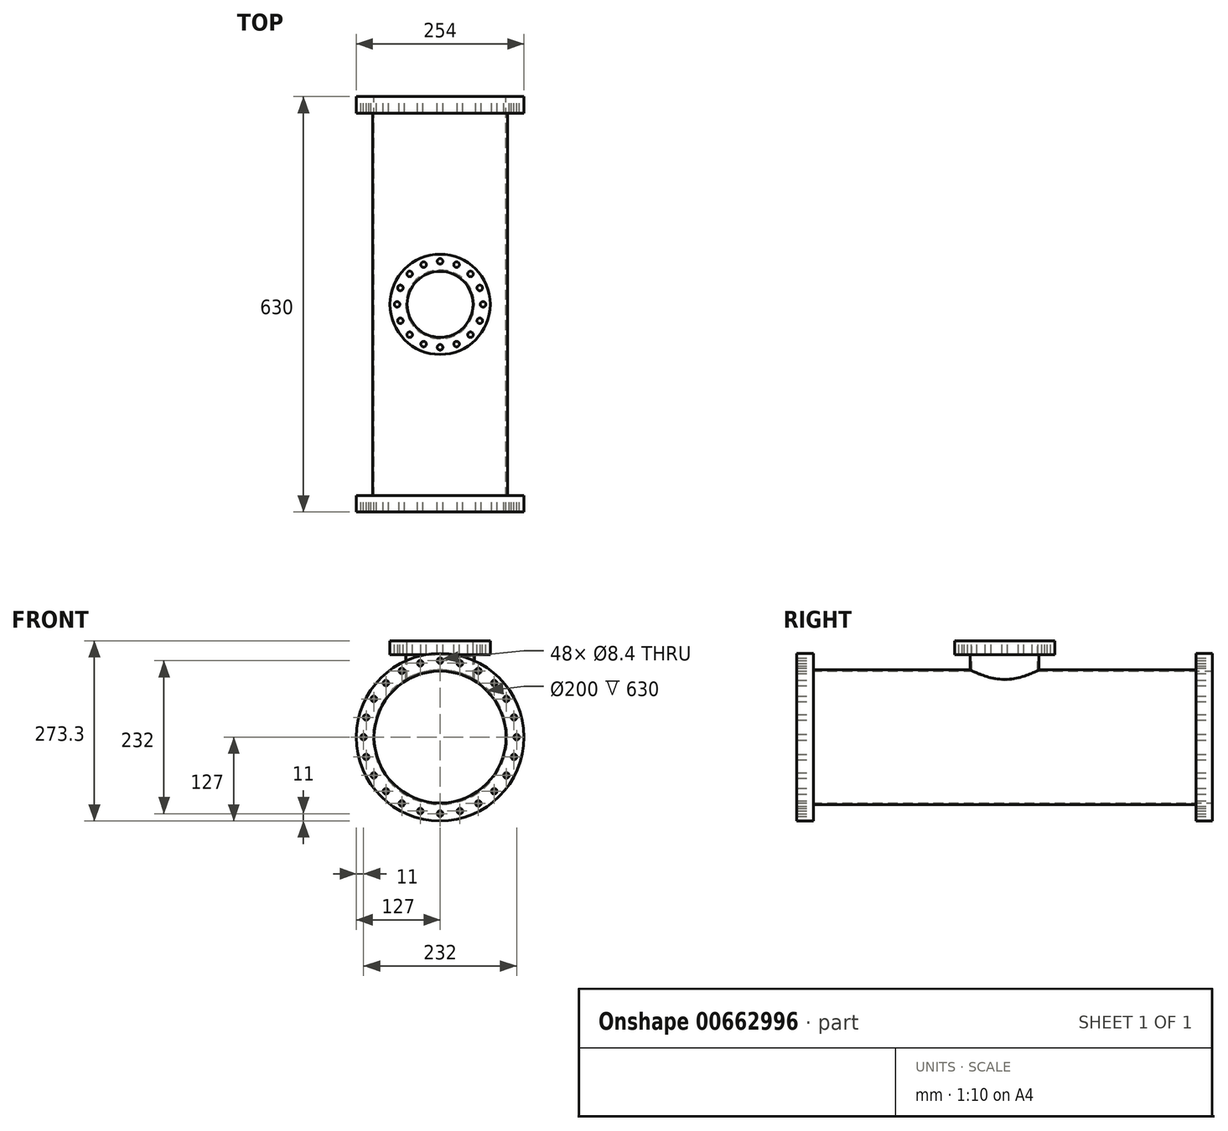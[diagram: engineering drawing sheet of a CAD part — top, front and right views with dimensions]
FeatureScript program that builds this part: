
annotation { "Feature Type Name" : "Feature", "Feature Type Description" : "" }
export const myFeature = defineFeature(function(context is Context, id is Id, definition is map)
    precondition{}
    {
        {
            var Q0;
            Q0=qCreatedBy(makeId("Front.planeOp"),FACE);
            var sketch = newSketch(context, id + "F0", { "sketchPlane" : qUnion([Q0])});
            skCircle(sketch, "E0", {"center": v(0, 0) * mm, "radius": 100 * mm});
            skCircle(sketch, "E1.0", {"center": v(0, 0) * mm, "radius": 102 * mm});
            skSolve(sketch);
        }
        {
            var Q0;
            Q0=makeQuery(id+"F0.imprint","IMPRINT",FACE,{"disambiguationData":[TD([[makeQuery(id+"F0.imprint","IMPRINT",EDGE,{"derivedFrom":sQuery(id+"F0.wireOp",EDGE,"E0")}),-1.0]])]});
            extrude(context, id + "F1", {"entities" : qUnion([Q0]), "depth" : (630 - 50) * mm, "offsetDistance" : 25 * mm});
        }
        {
            var Q0;
            Q0=makeQuery(id+"F1.opExtrude","CAP_FACE",FACE,{"disambiguationData":[OSD([sQuery(id+"F0.wireOp",EDGE,"E0"),sQuery(id+"F0.wireOp",EDGE,"E1.0")])],"isStart":false});
            var sketch = newSketch(context, id + "F2", { "sketchPlane" : qUnion([Q0])});
            skCircle(sketch, "E2", {"center": v(0, 0) * mm, "radius": 127 * mm});
            skSolve(sketch);
        }
        {
            var Q0;
            Q0=makeQuery(id+"F2.imprint","IMPRINT",FACE,{"disambiguationData":[TD([[makeQuery(id+"F2.imprint","IMPRINT",EDGE,{"derivedFrom":makeQuery(id+"F1.opExtrude","CAP_EDGE",EDGE,{"disambiguationData":[OSD([sQuery(id+"F0.wireOp",EDGE,"E0")])],"isStart":false})}),-1.0]])]});
            var Q1;
            Q1=makeQuery(id+"F2.imprint","IMPRINT",FACE,{"disambiguationData":[TD([[makeQuery(id+"F2.imprint","IMPRINT",EDGE,{"derivedFrom":sQuery(id+"F2.wireOp",EDGE,"E2")}),1.0]])]});
            extrude(context, id + "F3", {"entities" : qUnion([Q0, Q1]), "operationType" : NewBodyOperationType.ADD, "depth" : 25 * mm, "offsetDistance" : 25 * mm});
        }
        {
            var Q0;
            Q0=makeQuery(id+"F1.opExtrude","CAP_FACE",FACE,{"disambiguationData":[OSD([sQuery(id+"F0.wireOp",EDGE,"E0"),sQuery(id+"F0.wireOp",EDGE,"E1.0")])],"isStart":true});
            var sketch = newSketch(context, id + "F4", { "sketchPlane" : qUnion([Q0])});
            skCircle(sketch, "E3", {"center": v(0, 0) * mm, "radius": 127 * mm});
            skSolve(sketch);
        }
        {
            var Q0;
            Q0=makeQuery(id+"F4.imprint","IMPRINT",FACE,{"disambiguationData":[TD([[makeQuery(id+"F4.imprint","IMPRINT",EDGE,{"derivedFrom":makeQuery(id+"F1.opExtrude","CAP_EDGE",EDGE,{"disambiguationData":[OSD([sQuery(id+"F0.wireOp",EDGE,"E0")])],"isStart":true})}),1.0]])]});
            var Q1;
            Q1=makeQuery(id+"F4.imprint","IMPRINT",FACE,{"disambiguationData":[TD([[makeQuery(id+"F4.imprint","IMPRINT",EDGE,{"derivedFrom":sQuery(id+"F4.wireOp",EDGE,"E3")}),1.0]])]});
            extrude(context, id + "F5", {"entities" : qUnion([Q0, Q1]), "operationType" : NewBodyOperationType.ADD, "depth" : 25 * mm, "offsetDistance" : 25 * mm});
        }
        {
            var Q0;
            Q0=makeQuery(id+"F5.opExtrude","CAP_FACE",FACE,{"disambiguationData":[OSD([sQuery(id+"F0.wireOp",EDGE,"E0"),sQuery(id+"F4.wireOp",EDGE,"E3")])],"isStart":false});
            var sketch = newSketch(context, id + "F6", { "sketchPlane" : qUnion([Q0])});
            skCircle(sketch, "E4", {"center": v(0, 0) * mm, "radius": 116 * mm, "construction": true});
            skPoint(sketch, "E5", {"position": v(0, 116) * mm});
            skPoint(sketch, "E6.1.0", {"position": v(-30.02, 112.05) * mm});
            skPoint(sketch, "E6.2.0", {"position": v(-58, 100.46) * mm});
            skPoint(sketch, "E6.3.0", {"position": v(-82.02, 82.02) * mm});
            skPoint(sketch, "E6.4.0", {"position": v(-100.46, 58) * mm});
            skPoint(sketch, "E6.5.0", {"position": v(-112.05, 30.02) * mm});
            skPoint(sketch, "E6.6.0", {"position": v(-116, 0) * mm});
            skPoint(sketch, "E6.7.0", {"position": v(-112.05, -30.02) * mm});
            skPoint(sketch, "E6.8.0", {"position": v(-100.46, -58) * mm});
            skPoint(sketch, "E6.9.0", {"position": v(-82.02, -82.02) * mm});
            skPoint(sketch, "E6.10.0", {"position": v(-58, -100.46) * mm});
            skPoint(sketch, "E6.11.0", {"position": v(-30.02, -112.05) * mm});
            skPoint(sketch, "E6.12.0", {"position": v(0, -116) * mm});
            skPoint(sketch, "E6.13.0", {"position": v(30.02, -112.05) * mm});
            skPoint(sketch, "E6.14.0", {"position": v(58, -100.46) * mm});
            skPoint(sketch, "E6.15.0", {"position": v(82.02, -82.02) * mm});
            skPoint(sketch, "E6.16.0", {"position": v(100.46, -58) * mm});
            skPoint(sketch, "E6.17.0", {"position": v(112.05, -30.02) * mm});
            skPoint(sketch, "E6.18.0", {"position": v(116, 0) * mm});
            skPoint(sketch, "E6.19.0", {"position": v(112.05, 30.02) * mm});
            skPoint(sketch, "E6.20.0", {"position": v(100.46, 58) * mm});
            skPoint(sketch, "E6.21.0", {"position": v(82.02, 82.02) * mm});
            skPoint(sketch, "E6.22.0", {"position": v(58, 100.46) * mm});
            skPoint(sketch, "E6.23.0", {"position": v(30.02, 112.05) * mm});
            skSolve(sketch);
        }
        {
            var Q0;
            Q0=sQuery(id+"F6.wireOp",VERTEX,"E5");
            var Q1;
            Q1=sQuery(id+"F6.wireOp",VERTEX,"E6.23.0");
            var Q2;
            Q2=sQuery(id+"F6.wireOp",VERTEX,"E6.22.0");
            var Q3;
            Q3=sQuery(id+"F6.wireOp",VERTEX,"E6.21.0");
            var Q4;
            Q4=sQuery(id+"F6.wireOp",VERTEX,"E6.20.0");
            var Q5;
            Q5=sQuery(id+"F6.wireOp",VERTEX,"E6.19.0");
            var Q6;
            Q6=sQuery(id+"F6.wireOp",VERTEX,"E6.18.0");
            var Q7;
            Q7=sQuery(id+"F6.wireOp",VERTEX,"E6.17.0");
            var Q8;
            Q8=sQuery(id+"F6.wireOp",VERTEX,"E6.16.0");
            var Q9;
            Q9=sQuery(id+"F6.wireOp",VERTEX,"E6.15.0");
            var Q10;
            Q10=sQuery(id+"F6.wireOp",VERTEX,"E6.14.0");
            var Q11;
            Q11=sQuery(id+"F6.wireOp",VERTEX,"E6.13.0");
            var Q12;
            Q12=sQuery(id+"F6.wireOp",VERTEX,"E6.12.0");
            var Q13;
            Q13=sQuery(id+"F6.wireOp",VERTEX,"E6.11.0");
            var Q14;
            Q14=sQuery(id+"F6.wireOp",VERTEX,"E6.10.0");
            var Q15;
            Q15=sQuery(id+"F6.wireOp",VERTEX,"E6.9.0");
            var Q16;
            Q16=sQuery(id+"F6.wireOp",VERTEX,"E6.8.0");
            var Q17;
            Q17=sQuery(id+"F6.wireOp",VERTEX,"E6.7.0");
            var Q18;
            Q18=sQuery(id+"F6.wireOp",VERTEX,"E6.6.0");
            var Q19;
            Q19=sQuery(id+"F6.wireOp",VERTEX,"E6.5.0");
            var Q20;
            Q20=sQuery(id+"F6.wireOp",VERTEX,"E6.4.0");
            var Q21;
            Q21=sQuery(id+"F6.wireOp",VERTEX,"E6.3.0");
            var Q22;
            Q22=sQuery(id+"F6.wireOp",VERTEX,"E6.2.0");
            var Q23;
            Q23=sQuery(id+"F6.wireOp",VERTEX,"E6.1.0");
            var Q24;
            Q24=makeQuery(id+"F1.opExtrude","SWEPT_BODY",BODY,{"disambiguationData":[OSD([sQuery(id+"F0.wireOp",EDGE,"E0"),sQuery(id+"F0.wireOp",EDGE,"E1.0")])]});
            hole(context, id + "F7", {"style" : HoleStyle.SIMPLE, "endStyle" : HoleEndStyle.THROUGH, "standardTappedOrClearance" : lookupTablePath({ "fit" : "Close", "standard" : "ISO", "size" : "M8", "type" : "Clearance" }), "standardBlindInLast" : lookupTablePath({ "fit" : "Close", "standard" : "ISO", "engagement" : "75%", "pitch" : "1.25 mm", "size" : "M8", "type" : "Clearance & tapped" }), "holeDiameter" : 8.4 * mm, "majorDiameter" : 5 * mm, "isTappedThrough" : true, "tappedDepth" : 12 * mm, "tapClearance" : 3, "locations" : qUnion([Q0, Q1, Q2, Q3, Q4, Q5, Q6, Q7, Q8, Q9, Q10, Q11, Q12, Q13, Q14, Q15, Q16, Q17, Q18, Q19, Q20, Q21, Q22, Q23]), "scope" : qUnion([Q24])});
        }
        {
            var Q0;
            Q0=qCreatedBy(makeId("Top.planeOp"),FACE);
            cPlane(context, id + "F8", {"entities" : qUnion([Q0]), "cplaneType" : CPlaneType.OFFSET, "offset" : 125 * mm, "width" : 150 * mm, "height" : 150 * mm});
        }
        {
            var Q0;
            Q0=qCreatedBy(id+"F8.planeOp",FACE);
            var sketch = newSketch(context, id + "F9", { "sketchPlane" : qUnion([Q0])});
            skCircle(sketch, "E7", {"center": v(0, -290) * mm, "radius": 50 * mm});
            skLineSegment(sketch, "E8", {"start": v(0, 0) * mm, "end": v(0, -290) * mm, "construction": true});
            skLineSegment(sketch, "E9", {"start": v(0, -290) * mm, "end": v(0, -580) * mm, "construction": true});
            skCircle(sketch, "E10.0", {"center": v(0, -290) * mm, "radius": 52 * mm});
            skCircle(sketch, "E11", {"center": v(0, -290) * mm, "radius": 76 * mm});
            skSolve(sketch);
        }
        {
            var Q0;
            Q0=makeQuery(id+"F9.imprint","IMPRINT",FACE,{"disambiguationData":[TD([[makeQuery(id+"F9.imprint","IMPRINT",EDGE,{"derivedFrom":sQuery(id+"F9.wireOp",EDGE,"E7")}),-1.0]])]});
            var Q1;
            Q1=makeQuery(id+"F1.opExtrude","SWEPT_FACE",FACE,{"disambiguationData":[OSD([sQuery(id+"F0.wireOp",EDGE,"E1.0")])]});
            extrude(context, id + "F10", {"entities" : qUnion([Q0]), "operationType" : NewBodyOperationType.ADD, "endBound" : BoundingType.UP_TO_SURFACE, "oppositeDirection" : true, "depth" : 25 * mm, "endBoundEntityFace" : qUnion([Q1]), "offsetDistance" : 25 * mm});
        }
        {
            var Q0;
            Q0=makeQuery(id+"F9.imprint","IMPRINT",FACE,{"disambiguationData":[TD([[makeQuery(id+"F9.imprint","IMPRINT",EDGE,{"derivedFrom":sQuery(id+"F9.wireOp",EDGE,"E7")}),1.0]])]});
            var Q1;
            {var subQ0=sQuery(id+"F0.wireOp",EDGE,"E0");Q1=makeQuery(id+"F5.boolean.opBoolean","MERGE",FACE,{"derivedFrom":[makeQuery(id+"F3.boolean.opBoolean","MERGE",FACE,{"derivedFrom":[makeQuery(id+"F1.opExtrude","SWEPT_FACE",FACE,{"disambiguationData":[OSD([subQ0])]}),makeQuery(id+"F3.opExtrude","SWEPT_FACE",FACE,{"disambiguationData":[OSD([subQ0])]})]}),makeQuery(id+"F5.opExtrude","SWEPT_FACE",FACE,{"disambiguationData":[OSD([subQ0])]})]});}
            extrude(context, id + "F11", {"entities" : qUnion([Q0]), "operationType" : NewBodyOperationType.REMOVE, "endBound" : BoundingType.UP_TO_SURFACE, "oppositeDirection" : true, "depth" : 25 * mm, "endBoundEntityFace" : qUnion([Q1]), "offsetDistance" : 25 * mm});
        }
        {
            var Q0;
            Q0=makeQuery(id+"F9.imprint","IMPRINT",FACE,{"disambiguationData":[TD([[makeQuery(id+"F9.imprint","IMPRINT",EDGE,{"derivedFrom":sQuery(id+"F9.wireOp",EDGE,"E7")}),-1.0]])]});
            var Q1;
            Q1=makeQuery(id+"F9.imprint","IMPRINT",FACE,{"disambiguationData":[TD([[makeQuery(id+"F9.imprint","IMPRINT",EDGE,{"derivedFrom":sQuery(id+"F9.wireOp",EDGE,"E10.0")}),-1.0]])]});
            extrude(context, id + "F12", {"entities" : qUnion([Q0, Q1]), "operationType" : NewBodyOperationType.ADD, "depth" : 21.3 * mm, "offsetDistance" : 25 * mm});
        }
        {
            var Q0;
            Q0=makeQuery(id+"F12.opExtrude","CAP_FACE",FACE,{"disambiguationData":[OSD([sQuery(id+"F9.wireOp",EDGE,"E7"),sQuery(id+"F9.wireOp",EDGE,"E11")])],"isStart":false});
            var sketch = newSketch(context, id + "F13", { "sketchPlane" : qUnion([Q0])});
            skCircle(sketch, "E12", {"center": v(0, -290) * mm, "radius": 65.15 * mm, "construction": true});
            skPoint(sketch, "E13", {"position": v(0, -224.85) * mm});
            skPoint(sketch, "E14.1.0", {"position": v(-24.93, -229.8) * mm});
            skPoint(sketch, "E14.2.0", {"position": v(-46.07, -243.93) * mm});
            skPoint(sketch, "E14.3.0", {"position": v(-60.2, -265.07) * mm});
            skPoint(sketch, "E14.4.0", {"position": v(-65.15, -290) * mm});
            skPoint(sketch, "E14.5.0", {"position": v(-60.2, -314.93) * mm});
            skPoint(sketch, "E14.6.0", {"position": v(-46.07, -336.07) * mm});
            skPoint(sketch, "E14.7.0", {"position": v(-24.93, -350.2) * mm});
            skPoint(sketch, "E14.8.0", {"position": v(0, -355.15) * mm});
            skPoint(sketch, "E14.9.0", {"position": v(24.93, -350.2) * mm});
            skPoint(sketch, "E14.10.0", {"position": v(46.07, -336.07) * mm});
            skPoint(sketch, "E14.11.0", {"position": v(60.2, -314.93) * mm});
            skPoint(sketch, "E14.12.0", {"position": v(65.15, -290) * mm});
            skPoint(sketch, "E14.13.0", {"position": v(60.2, -265.07) * mm});
            skPoint(sketch, "E14.14.0", {"position": v(46.07, -243.93) * mm});
            skPoint(sketch, "E14.15.0", {"position": v(24.93, -229.8) * mm});
            skSolve(sketch);
        }
        {
            var Q0;
            Q0=sQuery(id+"F13.wireOp",VERTEX,"E13");
            var Q1;
            Q1=sQuery(id+"F13.wireOp",VERTEX,"E14.15.0");
            var Q2;
            Q2=sQuery(id+"F13.wireOp",VERTEX,"E14.14.0");
            var Q3;
            Q3=sQuery(id+"F13.wireOp",VERTEX,"E14.13.0");
            var Q4;
            Q4=sQuery(id+"F13.wireOp",VERTEX,"E14.12.0");
            var Q5;
            Q5=sQuery(id+"F13.wireOp",VERTEX,"E14.11.0");
            var Q6;
            Q6=sQuery(id+"F13.wireOp",VERTEX,"E14.10.0");
            var Q7;
            Q7=sQuery(id+"F13.wireOp",VERTEX,"E14.9.0");
            var Q8;
            Q8=sQuery(id+"F13.wireOp",VERTEX,"E14.8.0");
            var Q9;
            Q9=sQuery(id+"F13.wireOp",VERTEX,"E14.7.0");
            var Q10;
            Q10=sQuery(id+"F13.wireOp",VERTEX,"E14.6.0");
            var Q11;
            Q11=sQuery(id+"F13.wireOp",VERTEX,"E14.5.0");
            var Q12;
            Q12=sQuery(id+"F13.wireOp",VERTEX,"E14.4.0");
            var Q13;
            Q13=sQuery(id+"F13.wireOp",VERTEX,"E14.3.0");
            var Q14;
            Q14=sQuery(id+"F13.wireOp",VERTEX,"E14.2.0");
            var Q15;
            Q15=sQuery(id+"F13.wireOp",VERTEX,"E14.1.0");
            var Q16;
            Q16=makeQuery(id+"F1.opExtrude","SWEPT_BODY",BODY,{"disambiguationData":[OSD([sQuery(id+"F0.wireOp",EDGE,"E0"),sQuery(id+"F0.wireOp",EDGE,"E1.0")])]});
            hole(context, id + "F14", {"style" : HoleStyle.SIMPLE, "endStyle" : HoleEndStyle.BLIND, "standardTappedOrClearance" : lookupTablePath({ "fit" : "Close", "standard" : "ISO", "size" : "M8", "type" : "Clearance" }), "standardBlindInLast" : lookupTablePath({ "fit" : "Close", "standard" : "ISO", "engagement" : "75%", "pitch" : "1.25 mm", "size" : "M8", "type" : "Clearance & tapped" }), "holeDiameter" : 8.4 * mm, "majorDiameter" : 8 * mm, "holeDepth" : 27 * mm, "isTappedThrough" : true, "tappedDepth" : 12 * mm, "tapClearance" : 3, "locations" : qUnion([Q0, Q1, Q2, Q3, Q4, Q5, Q6, Q7, Q8, Q9, Q10, Q11, Q12, Q13, Q14, Q15]), "scope" : qUnion([Q16])});
        }
    });
